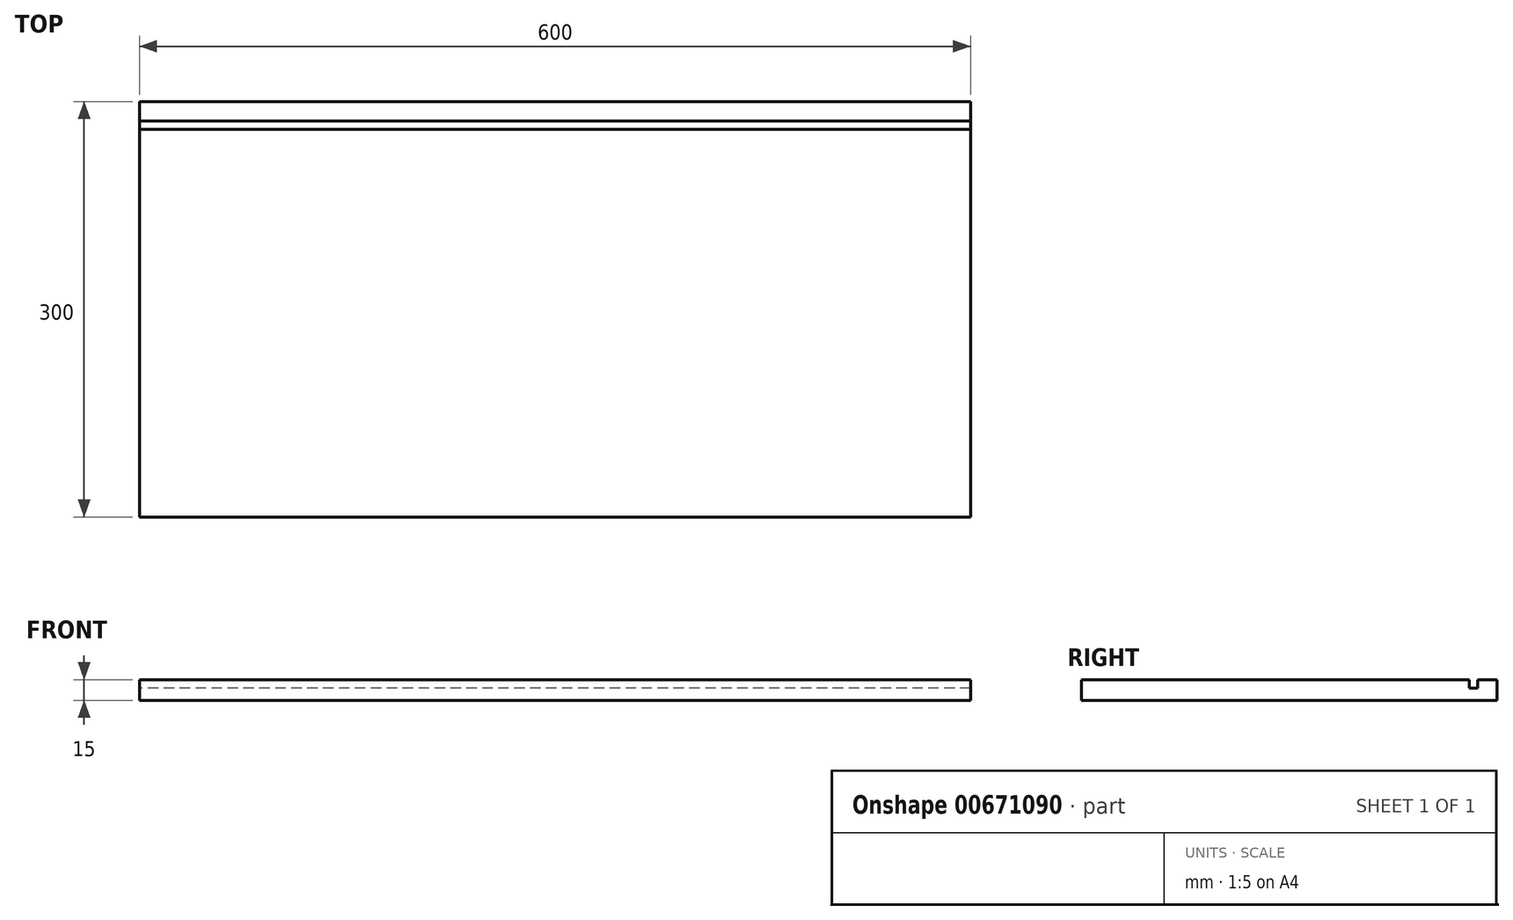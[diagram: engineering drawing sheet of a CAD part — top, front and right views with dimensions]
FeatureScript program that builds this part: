
annotation { "Feature Type Name" : "Feature", "Feature Type Description" : "" }
export const myFeature = defineFeature(function(context is Context, id is Id, definition is map)
    precondition{}
    {
        {
            var Q0;
            Q0=qCreatedBy(makeId("Top.planeOp"),FACE);
            var sketch = newSketch(context, id + "F0", { "sketchPlane" : qUnion([Q0])});
            skLineSegment(sketch, "E0.bottom", {"start": v(0, 0) * mm, "end": v(600, 0) * mm});
            skLineSegment(sketch, "E0.top", {"start": v(0, -300) * mm, "end": v(600, -300) * mm});
            skLineSegment(sketch, "E0.left", {"start": v(0, 0) * mm, "end": v(0, -300) * mm});
            skLineSegment(sketch, "E0.right", {"start": v(600, 0) * mm, "end": v(600, -300) * mm});
            skSolve(sketch);
        }
        {
            var Q0;
            Q0=makeQuery(id+"F0.imprint","IMPRINT",FACE,{"disambiguationData":[TD([[makeQuery(id+"F0.imprint","IMPRINT",EDGE,{"derivedFrom":sQuery(id+"F0.wireOp",EDGE,"E0.bottom")}),-1.0]])]});
            extrude(context, id + "F1", {"entities" : qUnion([Q0]), "depth" : 15 * mm, "offsetDistance" : 25 * mm});
        }
        {
            var Q0;
            Q0=makeQuery(id+"F1.opExtrude","SWEPT_FACE",FACE,{"disambiguationData":[OSD([sQuery(id+"F0.wireOp",EDGE,"E0.left")])]});
            var sketch = newSketch(context, id + "F2", { "sketchPlane" : qUnion([Q0])});
            skLineSegment(sketch, "E1.bottom", {"start": v(14, 15) * mm, "end": v(20, 15) * mm});
            skLineSegment(sketch, "E1.top", {"start": v(14, 9) * mm, "end": v(20, 9) * mm});
            skLineSegment(sketch, "E1.left", {"start": v(14, 15) * mm, "end": v(14, 9) * mm});
            skLineSegment(sketch, "E1.right", {"start": v(20, 15) * mm, "end": v(20, 9) * mm});
            skSolve(sketch);
        }
        {
            var Q0;
            Q0 = qSketchRegion(id + "F2", true);
            var Q1;
            Q1=makeQuery(id+"F2.imprint","IMPRINT",FACE,{"disambiguationData":[TD([[makeQuery(id+"F2.imprint","IMPRINT",EDGE,{"derivedFrom":sQuery(id+"F2.wireOp",EDGE,"E1.bottom")}),-1.0]])]});
            extrude(context, id + "F3", {"entities" : qUnion([Q0, Q1]), "operationType" : NewBodyOperationType.REMOVE, "oppositeDirection" : true, "depth" : 600 * mm, "offsetDistance" : 25 * mm});
        }
    });
